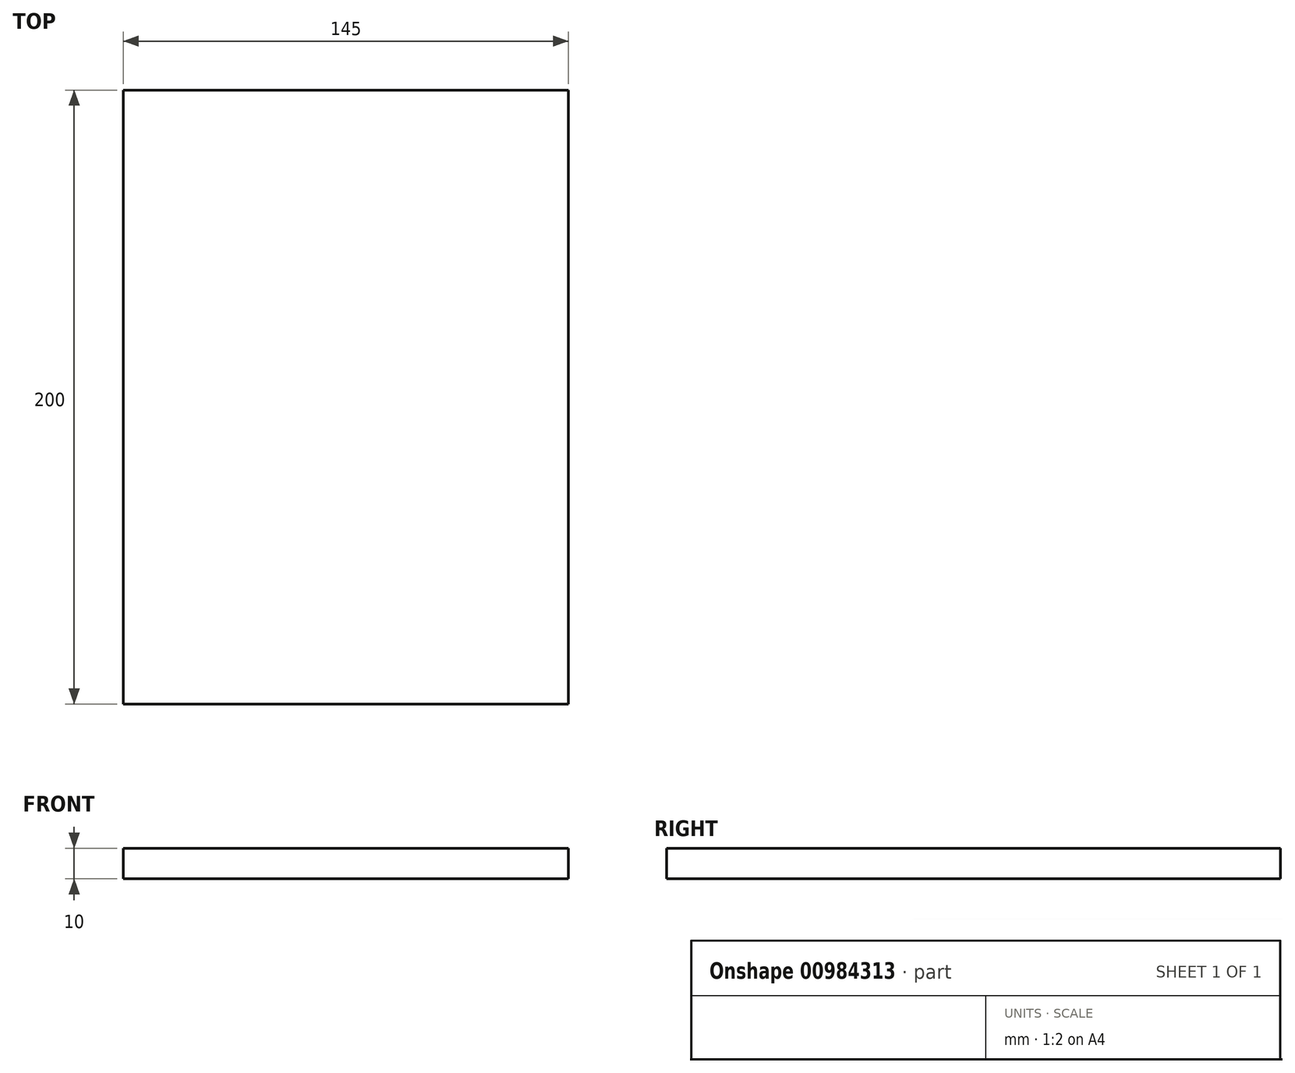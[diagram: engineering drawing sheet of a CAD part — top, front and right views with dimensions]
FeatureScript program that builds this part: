
annotation { "Feature Type Name" : "Feature", "Feature Type Description" : "" }
export const myFeature = defineFeature(function(context is Context, id is Id, definition is map)
    precondition{}
    {
        {
            var Q0;
            Q0=qCreatedBy(makeId("Top.planeOp"),FACE);
            var sketch = newSketch(context, id + "F0", { "sketchPlane" : qUnion([Q0])});
            skLineSegment(sketch, "E0.bottom", {"start": v(72.5, 100) * mm, "end": v(-72.5, 100) * mm});
            skLineSegment(sketch, "E0.top", {"start": v(72.5, -100) * mm, "end": v(-72.5, -100) * mm});
            skLineSegment(sketch, "E0.left", {"start": v(72.5, 100) * mm, "end": v(72.5, -100) * mm});
            skLineSegment(sketch, "E0.right", {"start": v(-72.5, 100) * mm, "end": v(-72.5, -100) * mm});
            skPoint(sketch, "E0.middle", {"position": v(0, 0) * mm});
            skSolve(sketch);
        }
        {
            var Q0;
            Q0=makeQuery(id+"F0.imprint","IMPRINT",FACE,{"disambiguationData":[TD([[makeQuery(id+"F0.imprint","IMPRINT",EDGE,{"derivedFrom":sQuery(id+"F0.wireOp",EDGE,"E0.bottom")}),1.0]])]});
            extrude(context, id + "F1", {"entities" : qUnion([Q0]), "depth" : 10 * mm, "offsetDistance" : 25 * mm});
        }
    });
